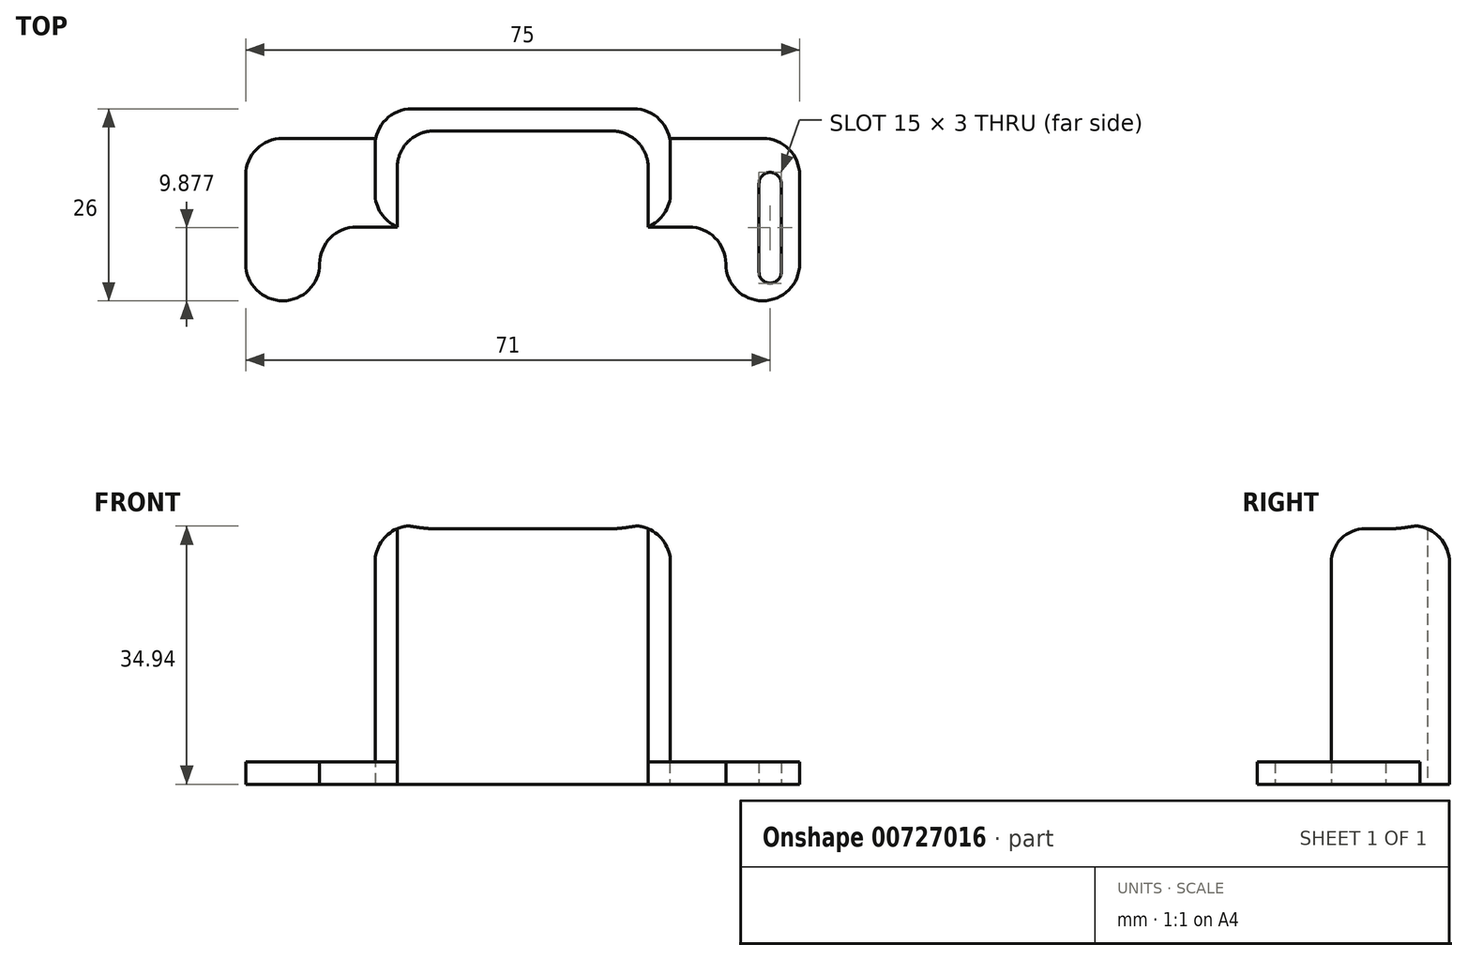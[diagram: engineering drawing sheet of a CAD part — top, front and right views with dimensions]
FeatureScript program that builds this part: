
annotation { "Feature Type Name" : "Feature", "Feature Type Description" : "" }
export const myFeature = defineFeature(function(context is Context, id is Id, definition is map)
    precondition{}
    {
        {
            var Q0;
            Q0=qCreatedBy(makeId("Top.planeOp"),FACE);
            var sketch = newSketch(context, id + "F0", { "sketchPlane" : qUnion([Q0])});
            skLineSegment(sketch, "E0", {"start": v(0, 26) * mm, "end": v(20, 26) * mm});
            skLineSegment(sketch, "E1", {"start": v(20, 26) * mm, "end": v(20, 22) * mm});
            skLineSegment(sketch, "E2", {"start": v(20, 22) * mm, "end": v(37.5, 22) * mm});
            skLineSegment(sketch, "E3", {"start": v(37.5, 22) * mm, "end": v(37.5, 0) * mm});
            skLineSegment(sketch, "E4", {"start": v(37.5, 0) * mm, "end": v(27.5, 0) * mm});
            skLineSegment(sketch, "E5", {"start": v(27.5, 0) * mm, "end": v(27.5, 10) * mm});
            skLineSegment(sketch, "E6", {"start": v(27.5, 10) * mm, "end": v(17, 10) * mm});
            skLineSegment(sketch, "E7", {"start": v(17, 10) * mm, "end": v(17, 23) * mm});
            skLineSegment(sketch, "E8", {"start": v(17, 23) * mm, "end": v(0, 23) * mm});
            skLineSegment(sketch, "E9.MirrorCS", {"start": v(0, 26) * mm, "end": v(-20, 26) * mm});
            skLineSegment(sketch, "E10.MirrorCS", {"start": v(-17, 23) * mm, "end": v(0, 23) * mm});
            skLineSegment(sketch, "E11.MirrorCS", {"start": v(-20, 26) * mm, "end": v(-20, 22) * mm});
            skLineSegment(sketch, "E12.MirrorCS", {"start": v(-17, 10) * mm, "end": v(-17, 23) * mm});
            skLineSegment(sketch, "E13.MirrorCS", {"start": v(-20, 22) * mm, "end": v(-37.5, 22) * mm});
            skLineSegment(sketch, "E14.MirrorCS", {"start": v(-27.5, 10) * mm, "end": v(-17, 10) * mm});
            skLineSegment(sketch, "E15.MirrorCS", {"start": v(-37.5, 22) * mm, "end": v(-37.5, 0) * mm});
            skLineSegment(sketch, "E16.MirrorCS", {"start": v(-27.5, 0) * mm, "end": v(-27.5, 10) * mm});
            skLineSegment(sketch, "E17.MirrorCS", {"start": v(-37.5, 0) * mm, "end": v(-27.5, 0) * mm});
            skPoint(sketch, "E18.firstSnap0", {"position": v(-37.5, 11) * mm});
            skLineSegment(sketch, "E19", {"start": v(-20, 22) * mm, "end": v(-20, 10) * mm});
            skLineSegment(sketch, "E20", {"start": v(20, 22) * mm, "end": v(20, 10) * mm});
            skLineSegment(sketch, "E21", {"start": v(-20, 10) * mm, "end": v(-17, 10) * mm});
            skLineSegment(sketch, "E22", {"start": v(17, 10) * mm, "end": v(20, 10) * mm});
            skSolve(sketch);
        }
        {
            var Q0;
            Q0=qCreatedBy(makeId("Top.planeOp"),FACE);
            var sketch = newSketch(context, id + "F1", { "sketchPlane" : qUnion([Q0])});
            skLineSegment(sketch, "E23", {"start": v(-33.5, 15.88) * mm, "end": v(-33.5, 3.88) * mm});
            skArc(sketch, "E24.0.startCap", {"start": v(-35, 15.88) * mm, "mid": v(-33.5, 17.38) * mm, "end": v(-32, 15.88) * mm});
            skArc(sketch, "E24.0.endCap", {"start": v(-32, 3.88) * mm, "mid": v(-33.5, 2.38) * mm, "end": v(-35, 3.88) * mm});
            skLineSegment(sketch, "E24.0.left", {"start": v(-32, 15.88) * mm, "end": v(-32, 3.88) * mm});
            skLineSegment(sketch, "E24.0.right", {"start": v(-35, 15.88) * mm, "end": v(-35, 3.88) * mm});
            skLineSegment(sketch, "E25.MirrorCS", {"start": v(35, 15.88) * mm, "end": v(35, 3.88) * mm});
            skLineSegment(sketch, "E26.MirrorCS", {"start": v(32, 15.88) * mm, "end": v(32, 3.88) * mm});
            skLineSegment(sketch, "E27.MirrorCS", {"start": v(33.5, 15.88) * mm, "end": v(33.5, 3.88) * mm});
            skArc(sketch, "E28.MirrorCS", {"start": v(35, 15.88) * mm, "mid": v(33.5, 17.38) * mm, "end": v(32, 15.88) * mm});
            skArc(sketch, "E29.MirrorCS", {"start": v(32, 3.88) * mm, "mid": v(33.5, 2.38) * mm, "end": v(35, 3.88) * mm});
            skSolve(sketch);
        }
        {
            var Q0;
            Q0=makeQuery(id+"F0.imprint","IMPRINT",FACE,{"disambiguationData":[TD([[makeQuery(id+"F0.imprint","IMPRINT",EDGE,{"derivedFrom":sQuery(id+"F0.wireOp",EDGE,"E0")}),-1.0]])]});
            var Q1;
            Q1=sQuery(id+"F0.wireOp",EDGE,"E12.MirrorCS");
            var Q2;
            Q2=sQuery(id+"F0.wireOp",EDGE,"E10.MirrorCS");
            var Q3;
            Q3=sQuery(id+"F0.wireOp",EDGE,"E8");
            var Q4;
            Q4=sQuery(id+"F0.wireOp",EDGE,"E7");
            var Q5;
            Q5=sQuery(id+"F0.wireOp",EDGE,"E1");
            var Q6;
            Q6=sQuery(id+"F0.wireOp",EDGE,"E20");
            var Q7;
            Q7=sQuery(id+"F0.wireOp",EDGE,"E0");
            var Q8;
            Q8=sQuery(id+"F0.wireOp",EDGE,"E9.MirrorCS");
            var Q9;
            Q9=sQuery(id+"F0.wireOp",EDGE,"E11.MirrorCS");
            var Q10;
            Q10=sQuery(id+"F0.wireOp",EDGE,"E19");
            var Q11;
            Q11=sQuery(id+"F0.wireOp",EDGE,"E21");
            var Q12;
            Q12=sQuery(id+"F0.wireOp",EDGE,"E22");
            extrude(context, id + "F2", {"entities" : qUnion([Q0]), "surfaceEntities" : qUnion([Q1, Q2, Q3, Q4, Q5, Q6, Q7, Q8, Q9, Q10, Q11, Q12]), "depth" : 35 * mm, "offsetDistance" : 25 * mm});
        }
        {
            var Q0;
            Q0=makeQuery(id+"F0.imprint","IMPRINT",FACE,{"disambiguationData":[TD([[makeQuery(id+"F0.imprint","IMPRINT",EDGE,{"derivedFrom":sQuery(id+"F0.wireOp",EDGE,"E13.MirrorCS")}),1.0]])]});
            var Q1;
            Q1=makeQuery(id+"F0.imprint","IMPRINT",FACE,{"disambiguationData":[TD([[makeQuery(id+"F0.imprint","IMPRINT",EDGE,{"derivedFrom":sQuery(id+"F0.wireOp",EDGE,"E2")}),-1.0]])]});
            extrude(context, id + "F3", {"entities" : qUnion([Q0, Q1]), "operationType" : NewBodyOperationType.ADD, "depth" : 3 * mm});
        }
        {
            var Q0;
            Q0=makeQuery(id+"F1.imprint","IMPRINT",FACE,{"disambiguationData":[TD([[makeQuery(id+"F1.imprint","IMPRINT",EDGE,{"derivedFrom":sQuery(id+"F1.wireOp",EDGE,"E25.MirrorCS")}),-1.0]])]});
            var Q1;
            Q1=makeQuery(id+"F1.imprint","IMPRINT",FACE,{"disambiguationData":[TD([[makeQuery(id+"F1.imprint","IMPRINT",EDGE,{"derivedFrom":sQuery(id+"F1.wireOp",EDGE,"E24.0.startCap")}),-1.0]])]});
            extrude(context, id + "F4", {"entities" : qUnion([Q0, Q1]), "operationType" : NewBodyOperationType.REMOVE, "depth" : 25 * mm});
        }
        {
            var Q0;
            Q0=makeQuery(id+"F3.opExtrude","SWEPT_EDGE",EDGE,{"disambiguationData":[OSD([sQuery(id+"F0.wireOp",EDGE,"E15.MirrorCS"),sQuery(id+"F0.wireOp",EDGE,"E17.MirrorCS")])]});
            var Q1;
            Q1=makeQuery(id+"F3.opExtrude","SWEPT_EDGE",EDGE,{"disambiguationData":[OSD([sQuery(id+"F0.wireOp",EDGE,"E16.MirrorCS"),sQuery(id+"F0.wireOp",EDGE,"E17.MirrorCS")])]});
            var Q2;
            Q2=makeQuery(id+"F3.opExtrude","SWEPT_EDGE",EDGE,{"disambiguationData":[OSD([sQuery(id+"F0.wireOp",EDGE,"E13.MirrorCS"),sQuery(id+"F0.wireOp",EDGE,"E15.MirrorCS")])]});
            var Q3;
            Q3=makeQuery(id+"F3.opExtrude","SWEPT_EDGE",EDGE,{"disambiguationData":[OSD([sQuery(id+"F0.wireOp",EDGE,"E2"),sQuery(id+"F0.wireOp",EDGE,"E3")])]});
            var Q4;
            Q4=makeQuery(id+"F3.opExtrude","SWEPT_EDGE",EDGE,{"disambiguationData":[OSD([sQuery(id+"F0.wireOp",EDGE,"E3"),sQuery(id+"F0.wireOp",EDGE,"E4")])]});
            var Q5;
            Q5=makeQuery(id+"F3.opExtrude","SWEPT_EDGE",EDGE,{"disambiguationData":[OSD([sQuery(id+"F0.wireOp",EDGE,"E4"),sQuery(id+"F0.wireOp",EDGE,"E5")])]});
            var Q6;
            Q6=makeQuery(id+"F3.opExtrude","SWEPT_EDGE",EDGE,{"disambiguationData":[OSD([sQuery(id+"F0.wireOp",EDGE,"E5"),sQuery(id+"F0.wireOp",EDGE,"E6")])]});
            var Q7;
            Q7=makeQuery(id+"F3.opExtrude","SWEPT_EDGE",EDGE,{"disambiguationData":[OSD([sQuery(id+"F0.wireOp",EDGE,"E14.MirrorCS"),sQuery(id+"F0.wireOp",EDGE,"E16.MirrorCS")])]});
            fillet(context, id + "F5", {"entities" : qUnion([Q0, Q1, Q2, Q3, Q4, Q5, Q6, Q7]), "radius" : 5 * mm, "tangentPropagation" : true, "allowEdgeOverflow" : false});
        }
        {
            var Q0;
            Q0=makeQuery(id+"F2.opExtrude","SWEPT_EDGE",EDGE,{"disambiguationData":[OSD([sQuery(id+"F0.wireOp",EDGE,"E0"),sQuery(id+"F0.wireOp",EDGE,"E1")])]});
            var Q1;
            Q1=makeQuery(id+"F2.opExtrude","SWEPT_EDGE",EDGE,{"disambiguationData":[OSD([sQuery(id+"F0.wireOp",EDGE,"E9.MirrorCS"),sQuery(id+"F0.wireOp",EDGE,"E11.MirrorCS")])]});
            var Q2;
            Q2=makeQuery(id+"F2.opExtrude","SWEPT_EDGE",EDGE,{"disambiguationData":[OSD([sQuery(id+"F0.wireOp",EDGE,"E14.MirrorCS"),sQuery(id+"F0.wireOp",EDGE,"E19")])]});
            var Q3;
            Q3=makeQuery(id+"F2.opExtrude","SWEPT_EDGE",EDGE,{"disambiguationData":[OSD([sQuery(id+"F0.wireOp",EDGE,"E6"),sQuery(id+"F0.wireOp",EDGE,"E20")])]});
            var Q4;
            Q4=makeQuery(id+"F2.opExtrude","SWEPT_EDGE",EDGE,{"disambiguationData":[OSD([sQuery(id+"F0.wireOp",EDGE,"E10.MirrorCS"),sQuery(id+"F0.wireOp",EDGE,"E12.MirrorCS")])]});
            var Q5;
            Q5=makeQuery(id+"F2.opExtrude","SWEPT_EDGE",EDGE,{"disambiguationData":[OSD([sQuery(id+"F0.wireOp",EDGE,"E7"),sQuery(id+"F0.wireOp",EDGE,"E8")])]});
            fillet(context, id + "F6", {"entities" : qUnion([Q0, Q1, Q2, Q3, Q4, Q5]), "radius" : 5 * mm, "tangentPropagation" : true, "allowEdgeOverflow" : false});
        }
        {
            var Q0;
            Q0=makeQuery(id+"F2.opExtrude","CAP_EDGE",EDGE,{"disambiguationData":[OSD([sQuery(id+"F0.wireOp",EDGE,"E11.MirrorCS"),sQuery(id+"F0.wireOp",EDGE,"E19")])],"isStart":false});
            fillet(context, id + "F7", {"entities" : qUnion([Q0]), "radius" : 5 * mm, "tangentPropagation" : true, "allowEdgeOverflow" : false});
        }
    });
